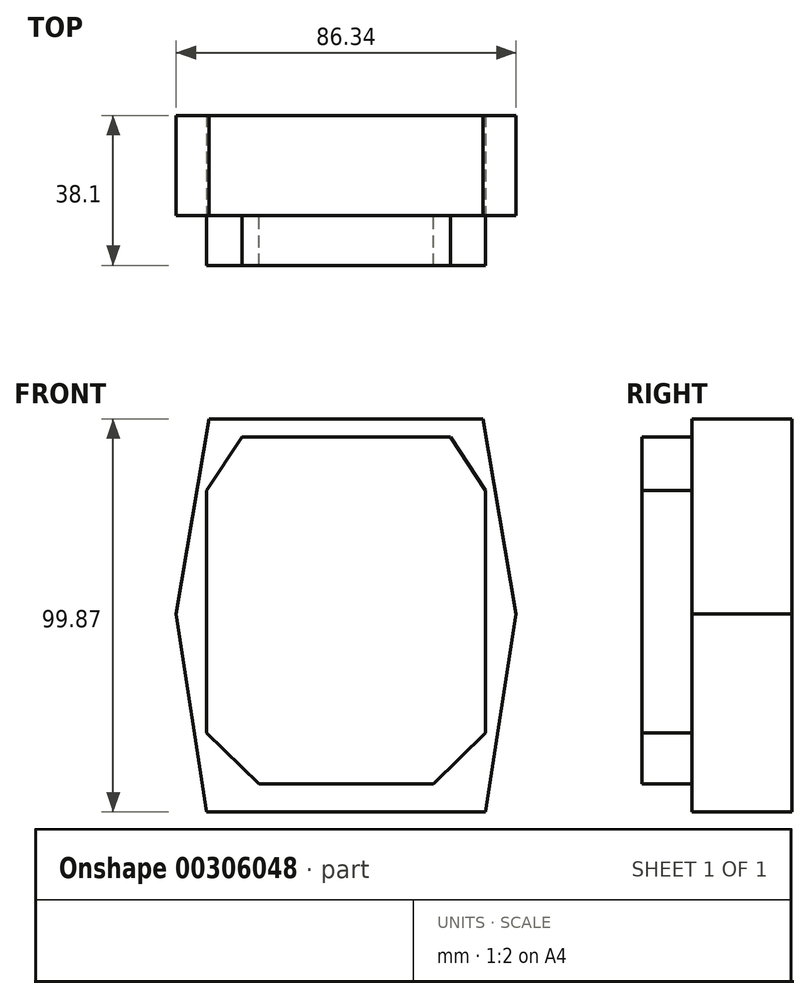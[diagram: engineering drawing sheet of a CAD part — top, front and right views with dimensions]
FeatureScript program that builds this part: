
annotation { "Feature Type Name" : "Feature", "Feature Type Description" : "" }
export const myFeature = defineFeature(function(context is Context, id is Id, definition is map)
    precondition{}
    {
        {
            var Q0;
            Q0=qCreatedBy(makeId("Front.planeOp"),FACE);
            var sketch = newSketch(context, id + "F0", { "sketchPlane" : qUnion([Q0])});
            skLineSegment(sketch, "E0", {"start": v(0, -43.17) * mm, "end": v(-22.16, -43.17) * mm});
            skLineSegment(sketch, "E1", {"start": v(-22.16, -43.17) * mm, "end": v(-35.4, -30.22) * mm});
            skLineSegment(sketch, "E2", {"start": v(-35.4, -30.22) * mm, "end": v(-35.4, 31.37) * mm});
            skLineSegment(sketch, "E3", {"start": v(-35.4, 31.37) * mm, "end": v(-26.48, 44.9) * mm});
            skLineSegment(sketch, "E4", {"start": v(-26.48, 44.9) * mm, "end": v(0, 44.9) * mm});
            skLineSegment(sketch, "E5.MirrorCS", {"start": v(26.48, 44.9) * mm, "end": v(0, 44.9) * mm});
            skLineSegment(sketch, "E6.MirrorCS", {"start": v(35.4, 31.37) * mm, "end": v(26.48, 44.9) * mm});
            skLineSegment(sketch, "E7.MirrorCS", {"start": v(35.4, -30.22) * mm, "end": v(35.4, 31.37) * mm});
            skLineSegment(sketch, "E8.MirrorCS", {"start": v(22.16, -43.17) * mm, "end": v(35.4, -30.22) * mm});
            skLineSegment(sketch, "E9.MirrorCS", {"start": v(0, -43.17) * mm, "end": v(22.16, -43.17) * mm});
            skSolve(sketch);
        }
        {
            var Q0;
            Q0=makeQuery(id+"F0.imprint","IMPRINT",FACE,{"disambiguationData":[TD([[makeQuery(id+"F0.imprint","IMPRINT",EDGE,{"derivedFrom":sQuery(id+"F0.wireOp",EDGE,"E0")}),-1.0]])]});
            extrude(context, id + "F1", {"entities" : qUnion([Q0]), "depth" : 25.4 * mm});
        }
        {
            var Q0;
            Q0=makeQuery(id+"F1.opExtrude","CAP_FACE",FACE,{"disambiguationData":[OSD([sQuery(id+"F0.wireOp",EDGE,"E0"),sQuery(id+"F0.wireOp",EDGE,"E1"),sQuery(id+"F0.wireOp",EDGE,"E2"),sQuery(id+"F0.wireOp",EDGE,"E3"),sQuery(id+"F0.wireOp",EDGE,"E4"),sQuery(id+"F0.wireOp",EDGE,"E5.MirrorCS"),sQuery(id+"F0.wireOp",EDGE,"E6.MirrorCS"),sQuery(id+"F0.wireOp",EDGE,"E7.MirrorCS"),sQuery(id+"F0.wireOp",EDGE,"E8.MirrorCS"),sQuery(id+"F0.wireOp",EDGE,"E9.MirrorCS")])],"isStart":false});
            extrude(context, id + "F2", {"entities" : qUnion([Q0]), "operationType" : NewBodyOperationType.REMOVE, "oppositeDirection" : true, "depth" : 12.7 * mm});
        }
        {
            var Q0;
            Q0=qCreatedBy(makeId("Front.planeOp"),FACE);
            var sketch = newSketch(context, id + "F3", { "sketchPlane" : qUnion([Q0])});
            skLineSegment(sketch, "E10", {"start": v(0, 49.5) * mm, "end": v(-34.82, 49.5) * mm});
            skLineSegment(sketch, "E11", {"start": v(-34.82, 49.5) * mm, "end": v(-43.17, 0) * mm});
            skLineSegment(sketch, "E12", {"start": v(-43.17, 0) * mm, "end": v(-35.4, -50.37) * mm});
            skLineSegment(sketch, "E13", {"start": v(-35.4, -50.37) * mm, "end": v(0, -50.37) * mm});
            skLineSegment(sketch, "E14.MirrorCS", {"start": v(-43.17, 99) * mm, "end": v(-35.4, 149.37) * mm});
            skLineSegment(sketch, "E15.MirrorCS", {"start": v(-35.4, 149.37) * mm, "end": v(0, 149.37) * mm});
            skLineSegment(sketch, "E16.MirrorCS", {"start": v(0, 49.5) * mm, "end": v(34.82, 49.5) * mm});
            skLineSegment(sketch, "E17.MirrorCS", {"start": v(34.82, 49.5) * mm, "end": v(43.17, 0) * mm});
            skLineSegment(sketch, "E18.MirrorCS", {"start": v(43.17, 0) * mm, "end": v(35.4, -50.37) * mm});
            skLineSegment(sketch, "E19.MirrorCS", {"start": v(35.4, -50.37) * mm, "end": v(0, -50.37) * mm});
            skSolve(sketch);
        }
        {
            var Q0;
            Q0=makeQuery(id+"F3.imprint","IMPRINT",FACE,{"disambiguationData":[TD([[makeQuery(id+"F3.imprint","IMPRINT",EDGE,{"derivedFrom":sQuery(id+"F3.wireOp",EDGE,"E10")}),1.0]])]});
            extrude(context, id + "F4", {"entities" : qUnion([Q0]), "operationType" : NewBodyOperationType.ADD, "oppositeDirection" : true, "depth" : 25.4 * mm});
        }
        {
            var Q0;
            Q0=makeQuery(id+"F2.boolean.opBoolean","COPY",FACE,{"derivedFrom":makeQuery(id+"F2.opExtrude","CAP_FACE",FACE,{"disambiguationData":[OSD([sQuery(id+"F0.wireOp",EDGE,"E0"),sQuery(id+"F0.wireOp",EDGE,"E1"),sQuery(id+"F0.wireOp",EDGE,"E2"),sQuery(id+"F0.wireOp",EDGE,"E3"),sQuery(id+"F0.wireOp",EDGE,"E4"),sQuery(id+"F0.wireOp",EDGE,"E5.MirrorCS"),sQuery(id+"F0.wireOp",EDGE,"E6.MirrorCS"),sQuery(id+"F0.wireOp",EDGE,"E7.MirrorCS"),sQuery(id+"F0.wireOp",EDGE,"E8.MirrorCS"),sQuery(id+"F0.wireOp",EDGE,"E9.MirrorCS")])],"isStart":false})});
            var sketch = newSketch(context, id + "F5", { "sketchPlane" : qUnion([Q0])});
            skLineSegment(sketch, "E20", {"start": v(22.16, -43.17) * mm, "end": v(35.4, -30.22) * mm});
            skLineSegment(sketch, "E21", {"start": v(35.4, -30.22) * mm, "end": v(35.4, 31.37) * mm});
            skLineSegment(sketch, "E22", {"start": v(35.4, 31.37) * mm, "end": v(26.48, 44.9) * mm});
            skLineSegment(sketch, "E23", {"start": v(26.48, 44.9) * mm, "end": v(-26.48, 44.9) * mm});
            skLineSegment(sketch, "E24", {"start": v(-26.48, 44.9) * mm, "end": v(-35.4, 31.37) * mm});
            skLineSegment(sketch, "E25", {"start": v(-35.4, 31.37) * mm, "end": v(-35.4, -30.22) * mm});
            skLineSegment(sketch, "E26", {"start": v(-35.4, -30.22) * mm, "end": v(-22.16, -43.17) * mm});
            skLineSegment(sketch, "E27", {"start": v(-22.16, -43.17) * mm, "end": v(22.16, -43.17) * mm});
            skSolve(sketch);
        }
        {
            var Q0;
            Q0=makeQuery(id+"F2.boolean.opBoolean","COPY",FACE,{"derivedFrom":makeQuery(id+"F2.opExtrude","CAP_FACE",FACE,{"disambiguationData":[OSD([sQuery(id+"F0.wireOp",EDGE,"E0"),sQuery(id+"F0.wireOp",EDGE,"E1"),sQuery(id+"F0.wireOp",EDGE,"E2"),sQuery(id+"F0.wireOp",EDGE,"E3"),sQuery(id+"F0.wireOp",EDGE,"E4"),sQuery(id+"F0.wireOp",EDGE,"E5.MirrorCS"),sQuery(id+"F0.wireOp",EDGE,"E6.MirrorCS"),sQuery(id+"F0.wireOp",EDGE,"E7.MirrorCS"),sQuery(id+"F0.wireOp",EDGE,"E8.MirrorCS"),sQuery(id+"F0.wireOp",EDGE,"E9.MirrorCS")])],"isStart":false})});
            var Q1;
            Q1=sQuery(id+"F5.wireOp",EDGE,"E20");
            var Q2;
            Q2=sQuery(id+"F5.wireOp",EDGE,"E21");
            var Q3;
            Q3=sQuery(id+"F5.wireOp",EDGE,"E22");
            var Q4;
            Q4=sQuery(id+"F5.wireOp",EDGE,"E23");
            var Q5;
            Q5=sQuery(id+"F5.wireOp",EDGE,"E24");
            var Q6;
            Q6=sQuery(id+"F5.wireOp",EDGE,"E25");
            var Q7;
            Q7=sQuery(id+"F5.wireOp",EDGE,"E26");
            var Q8;
            Q8=sQuery(id+"F5.wireOp",EDGE,"E27");
            extrude(context, id + "F6", {"entities" : qUnion([Q0]), "bodyType" : ToolBodyType.SURFACE, "operationType" : NewBodyOperationType.ADD, "surfaceEntities" : qUnion([Q1, Q2, Q3, Q4, Q5, Q6, Q7, Q8]), "depth" : 19.05 * mm});
        }
    });
